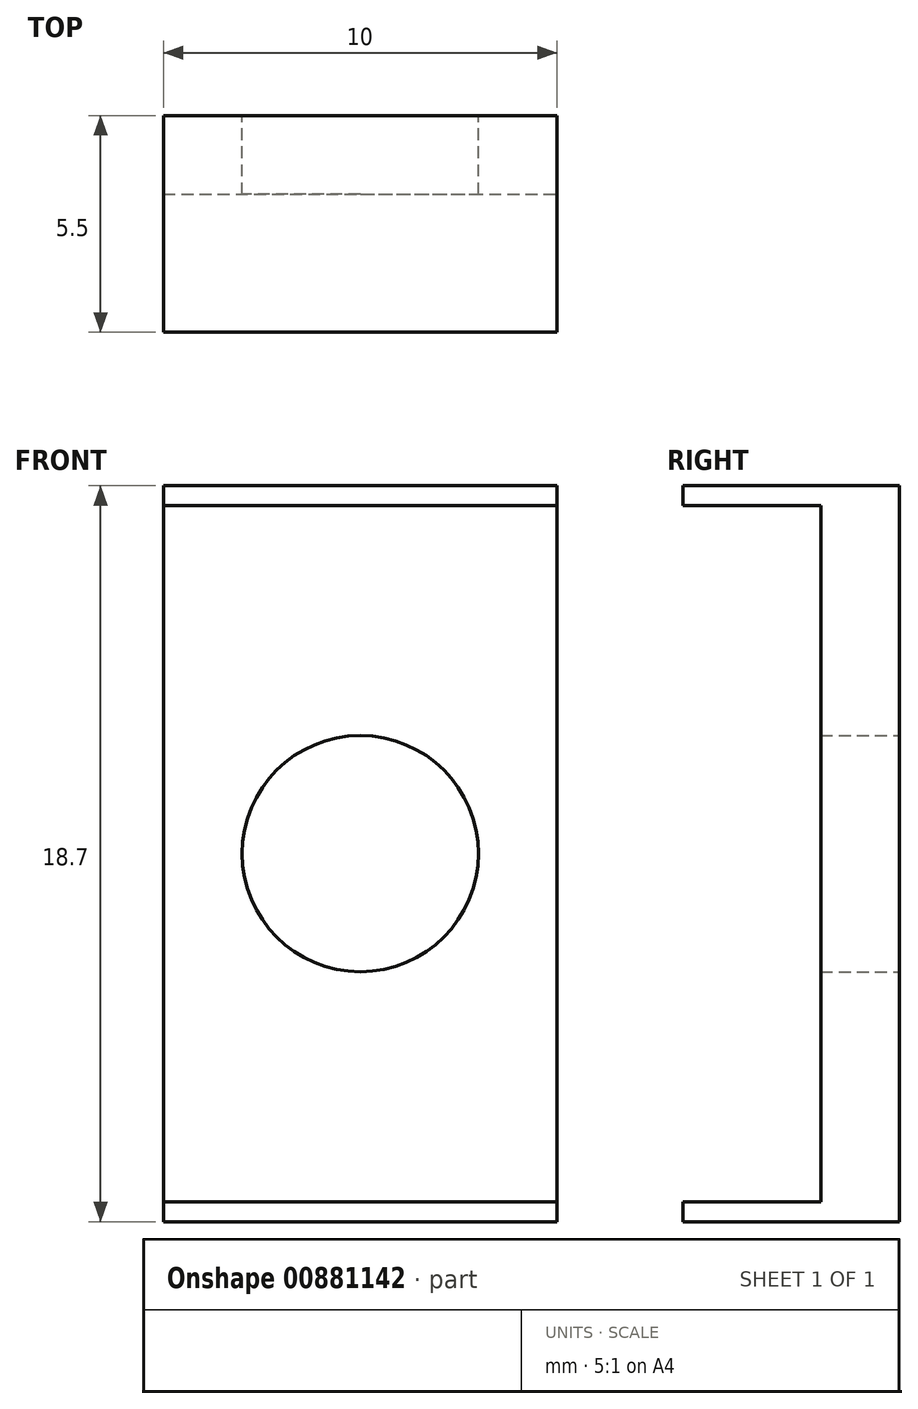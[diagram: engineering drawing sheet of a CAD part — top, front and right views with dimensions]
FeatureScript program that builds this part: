
annotation { "Feature Type Name" : "Feature", "Feature Type Description" : "" }
export const myFeature = defineFeature(function(context is Context, id is Id, definition is map)
    precondition{}
    {
        {
            var Q0;
            Q0=qCreatedBy(makeId("Front.planeOp"),FACE);
            var sketch = newSketch(context, id + "F0", { "sketchPlane" : qUnion([Q0])});
            skLineSegment(sketch, "E0.bottom", {"start": v(-5, -9.35) * mm, "end": v(5, -9.35) * mm});
            skLineSegment(sketch, "E0.top", {"start": v(-5, 9.35) * mm, "end": v(5, 9.35) * mm});
            skLineSegment(sketch, "E0.left", {"start": v(-5, -9.35) * mm, "end": v(-5, 9.35) * mm});
            skLineSegment(sketch, "E0.right", {"start": v(5, -9.35) * mm, "end": v(5, 9.35) * mm});
            skPoint(sketch, "E0.middle", {"position": v(0, 0) * mm});
            skSolve(sketch);
        }
        {
            var Q0;
            Q0=makeQuery(id+"F0.imprint","IMPRINT",FACE,{"disambiguationData":[TD([[makeQuery(id+"F0.imprint","IMPRINT",EDGE,{"derivedFrom":sQuery(id+"F0.wireOp",EDGE,"E0.bottom")}),1.0]])]});
            extrude(context, id + "F1", {"entities" : qUnion([Q0]), "depth" : 2 * mm, "offsetDistance" : 25 * mm});
        }
        {
            var Q0;
            Q0=makeQuery(id+"F1.opExtrude","CAP_FACE",FACE,{"disambiguationData":[OSD([sQuery(id+"F0.wireOp",EDGE,"E0.bottom"),sQuery(id+"F0.wireOp",EDGE,"E0.top"),sQuery(id+"F0.wireOp",EDGE,"E0.left"),sQuery(id+"F0.wireOp",EDGE,"E0.right")])],"isStart":false});
            var sketch = newSketch(context, id + "F2", { "sketchPlane" : qUnion([Q0])});
            skLineSegment(sketch, "E1.bottom", {"start": v(-5, 9.35) * mm, "end": v(5, 9.35) * mm});
            skLineSegment(sketch, "E1.top", {"start": v(-5, 8.85) * mm, "end": v(5, 8.85) * mm});
            skLineSegment(sketch, "E1.left", {"start": v(-5, 9.35) * mm, "end": v(-5, 8.85) * mm});
            skLineSegment(sketch, "E1.right", {"start": v(5, 9.35) * mm, "end": v(5, 8.85) * mm});
            skLineSegment(sketch, "E2.bottom", {"start": v(-5, 0) * mm, "end": v(5, 0) * mm, "construction": true});
            skLineSegment(sketch, "E2.top", {"start": v(-5, 0) * mm, "end": v(5, 0) * mm, "construction": true});
            skLineSegment(sketch, "E2.left", {"start": v(-5, 0) * mm, "end": v(-5, 0) * mm});
            skLineSegment(sketch, "E2.right", {"start": v(5, 0) * mm, "end": v(5, 0) * mm});
            skLineSegment(sketch, "E3.MirrorCS", {"start": v(-5, -9.35) * mm, "end": v(-5, -8.85) * mm});
            skLineSegment(sketch, "E4.MirrorCS", {"start": v(5, -9.35) * mm, "end": v(5, -8.85) * mm});
            skLineSegment(sketch, "E5.MirrorCS", {"start": v(-5, -8.85) * mm, "end": v(5, -8.85) * mm});
            skLineSegment(sketch, "E6.MirrorCS", {"start": v(-5, -9.35) * mm, "end": v(5, -9.35) * mm});
            skSolve(sketch);
        }
        {
            var Q0;
            Q0 = qSketchRegion(id + "F2", true);
            extrude(context, id + "F3", {"entities" : qUnion([Q0]), "operationType" : NewBodyOperationType.ADD, "depth" : 3.5 * mm, "offsetDistance" : 25 * mm});
        }
        {
            var Q0;
            Q0=makeQuery(id+"F1.opExtrude","CAP_FACE",FACE,{"disambiguationData":[OSD([sQuery(id+"F0.wireOp",EDGE,"E0.bottom"),sQuery(id+"F0.wireOp",EDGE,"E0.top"),sQuery(id+"F0.wireOp",EDGE,"E0.left"),sQuery(id+"F0.wireOp",EDGE,"E0.right")])],"isStart":true});
            var sketch = newSketch(context, id + "F4", { "sketchPlane" : qUnion([Q0])});
            skCircle(sketch, "E7", {"center": v(0, 0) * mm, "radius": 3 * mm});
            skSolve(sketch);
        }
        {
            var Q0;
            Q0 = qSketchRegion(id + "F4", true);
            extrude(context, id + "F5", {"entities" : qUnion([Q0]), "operationType" : NewBodyOperationType.REMOVE, "oppositeDirection" : true, "depth" : 25 * mm, "offsetDistance" : 25 * mm});
        }
    });
